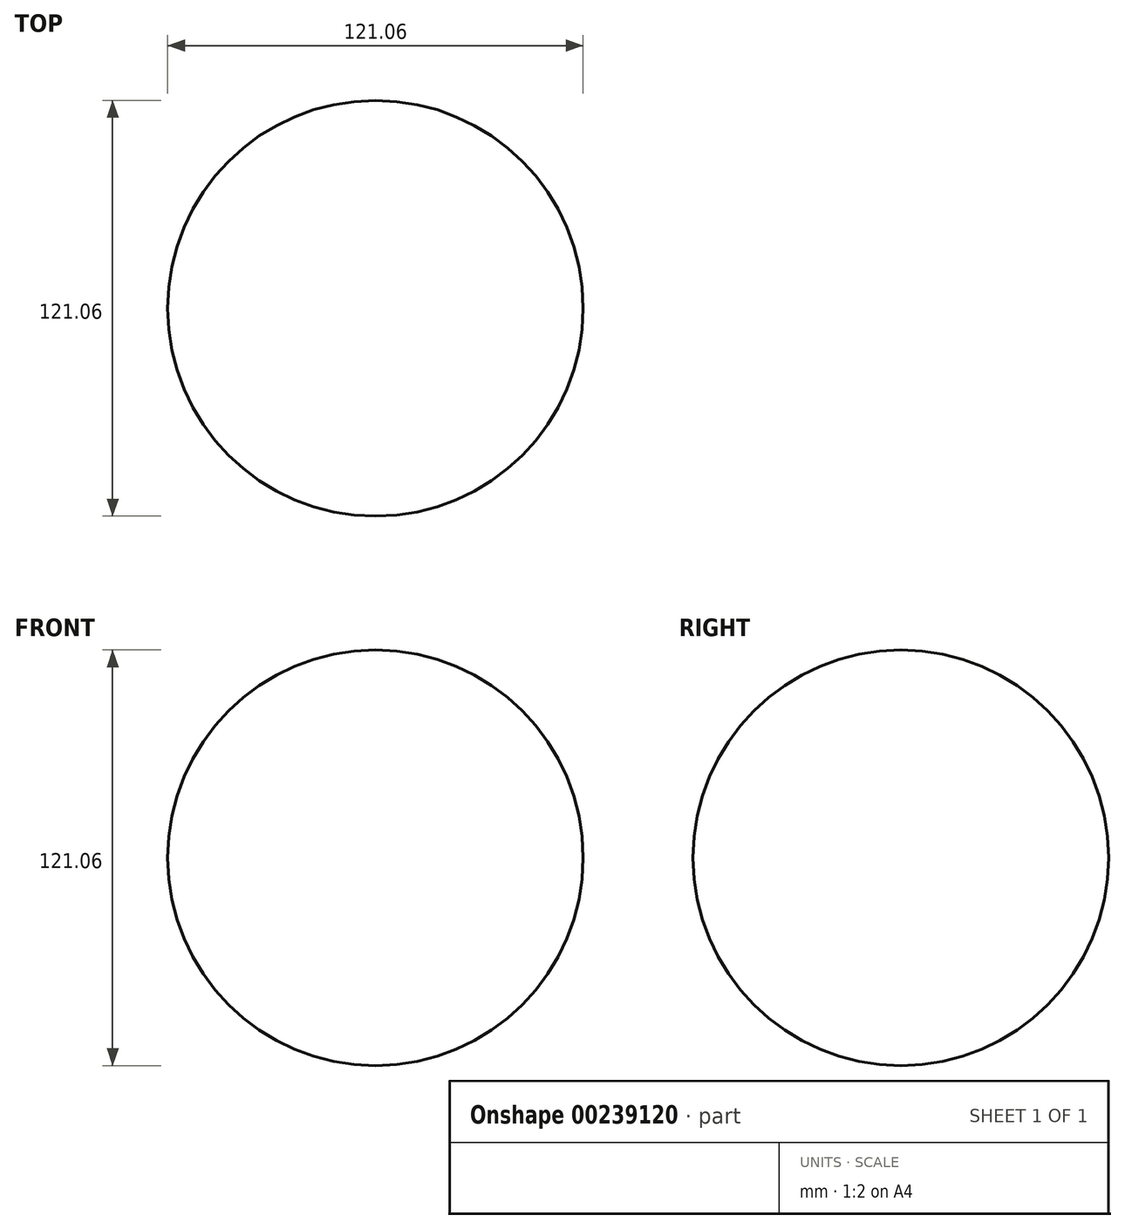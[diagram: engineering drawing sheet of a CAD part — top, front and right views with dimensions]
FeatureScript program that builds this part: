
annotation { "Feature Type Name" : "Feature", "Feature Type Description" : "" }
export const myFeature = defineFeature(function(context is Context, id is Id, definition is map)
    precondition{}
    {
        {
            var Q0;
            Q0=qCreatedBy(makeId("Front.planeOp"),FACE);
            var sketch = newSketch(context, id + "F0", { "sketchPlane" : qUnion([Q0])});
            skArc(sketch, "E0", {"start": v(0, -60.53) * mm, "mid": v(60.53, 0) * mm, "end": v(0, 60.53) * mm});
            skLineSegment(sketch, "E1", {"start": v(0, 60.53) * mm, "end": v(0, -60.53) * mm});
            skSolve(sketch);
        }
        {
            var Q0;
            Q0 = qSketchRegion(id + "F0", true);
            var Q1;
            Q1=sQuery(id+"F0.wireOp",EDGE,"E1");
            revolve(context, id + "F1", {"entities" : qUnion([Q0]), "axis" : qUnion([Q1]), "revolveType" : RevolveType.FULL});
        }
    });
